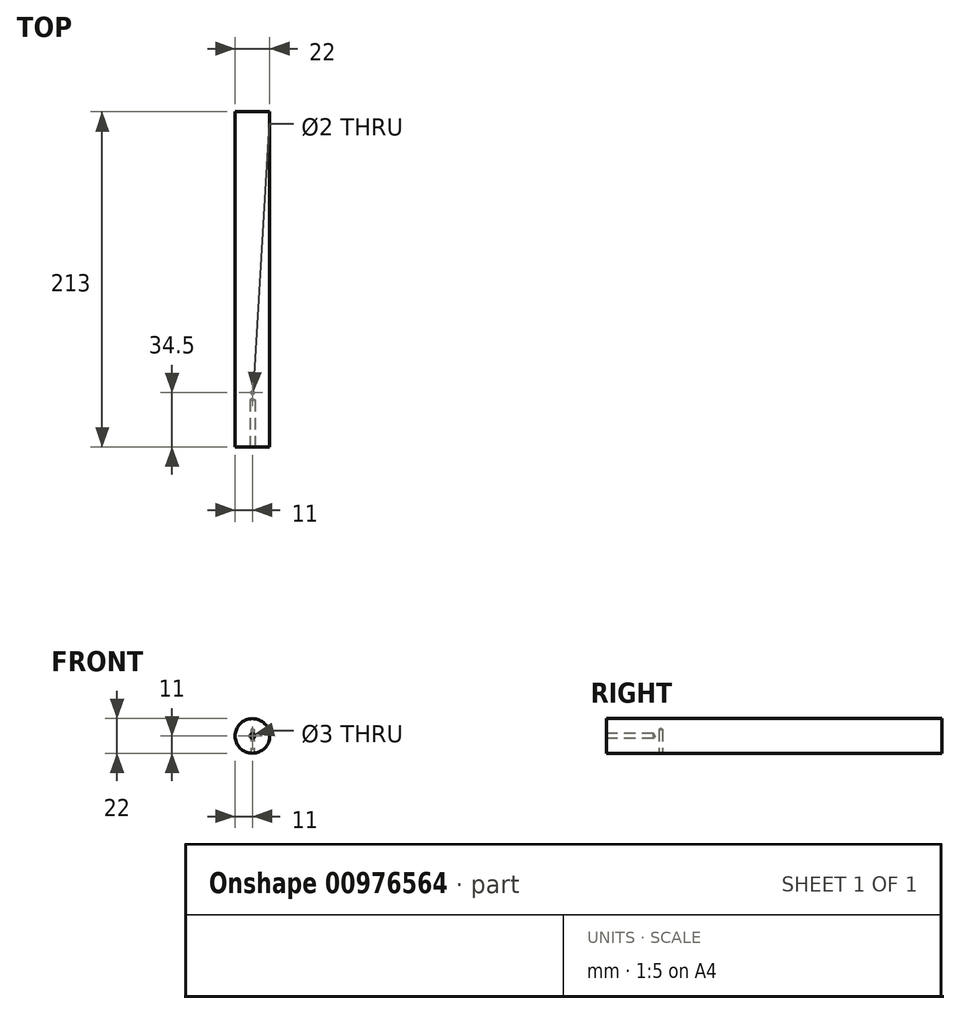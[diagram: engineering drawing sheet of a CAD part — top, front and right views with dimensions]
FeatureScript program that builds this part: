
annotation { "Feature Type Name" : "Feature", "Feature Type Description" : "" }
export const myFeature = defineFeature(function(context is Context, id is Id, definition is map)
    precondition{}
    {
        {
            var Q0;
            Q0=qCreatedBy(makeId("Front.planeOp"),FACE);
            var sketch = newSketch(context, id + "F0", { "sketchPlane" : qUnion([Q0])});
            skCircle(sketch, "E0", {"center": v(0, 11) * mm, "radius": 11 * mm});
            skLineSegment(sketch, "E1", {"start": v(0, 11) * mm, "end": v(0, 0) * mm, "construction": true});
            skLineSegment(sketch, "E2", {"start": v(0, 0) * mm, "end": v(22.65, 0) * mm, "construction": true});
            skSolve(sketch);
        }
        {
            var Q0;
            Q0=makeQuery(id+"F0.imprint","IMPRINT",FACE,{"disambiguationData":[TD([[makeQuery(id+"F0.imprint","IMPRINT",EDGE,{"derivedFrom":sQuery(id+"F0.wireOp",EDGE,"E0")}),1.0]])]});
            extrude(context, id + "F1", {"entities" : qUnion([Q0]), "endBound" : BoundingType.SYMMETRIC, "depth" : 213 * mm, "offsetDistance" : 25 * mm});
        }
        {
            var Q0;
            Q0=makeQuery(id+"F1.opExtrude","CAP_FACE",FACE,{"disambiguationData":[OSD([sQuery(id+"F0.wireOp",EDGE,"E0")])],"isStart":false});
            var sketch = newSketch(context, id + "F2", { "sketchPlane" : qUnion([Q0])});
            skPoint(sketch, "E3", {"position": v(0, 142.1) * mm});
            skPoint(sketch, "E4", {"position": v(0, 11) * mm});
            skSolve(sketch);
        }
        {
            var Q0;
            Q0=sQuery(id+"F2.wireOp",VERTEX,"E4");
            var Q1;
            Q1=makeQuery(id+"F1.opExtrude","SWEPT_BODY",BODY,{"disambiguationData":[OSD([sQuery(id+"F0.wireOp",EDGE,"E0")])]});
            hole(context, id + "F3", {"style" : HoleStyle.SIMPLE, "endStyle" : HoleEndStyle.BLIND, "holeDiameter" : 3 * mm, "majorDiameter" : 5 * mm, "holeDepth" : 30 * mm, "isTappedThrough" : true, "tappedDepth" : 12 * mm, "tapClearance" : 3, "locations" : qUnion([Q0]), "scope" : qUnion([Q1])});
        }
        {
            var Q0;
            Q0=qCreatedBy(makeId("Top.planeOp"),FACE);
            var sketch = newSketch(context, id + "F4", { "sketchPlane" : qUnion([Q0])});
            skPoint(sketch, "E5", {"position": v(0, -72) * mm});
            skSolve(sketch);
        }
        {
            var Q0;
            Q0=sQuery(id+"F4.wireOp",VERTEX,"E5");
            var Q1;
            Q1=makeQuery(id+"F1.opExtrude","SWEPT_BODY",BODY,{"disambiguationData":[OSD([sQuery(id+"F0.wireOp",EDGE,"E0")])]});
            hole(context, id + "F5", {"style" : HoleStyle.SIMPLE, "endStyle" : HoleEndStyle.BLIND, "oppositeDirection" : true, "holeDiameter" : 2 * mm, "majorDiameter" : 5 * mm, "holeDepth" : 15 * mm, "isTappedThrough" : true, "tappedDepth" : 12 * mm, "tapClearance" : 3, "locations" : qUnion([Q0]), "scope" : qUnion([Q1])});
        }
    });
